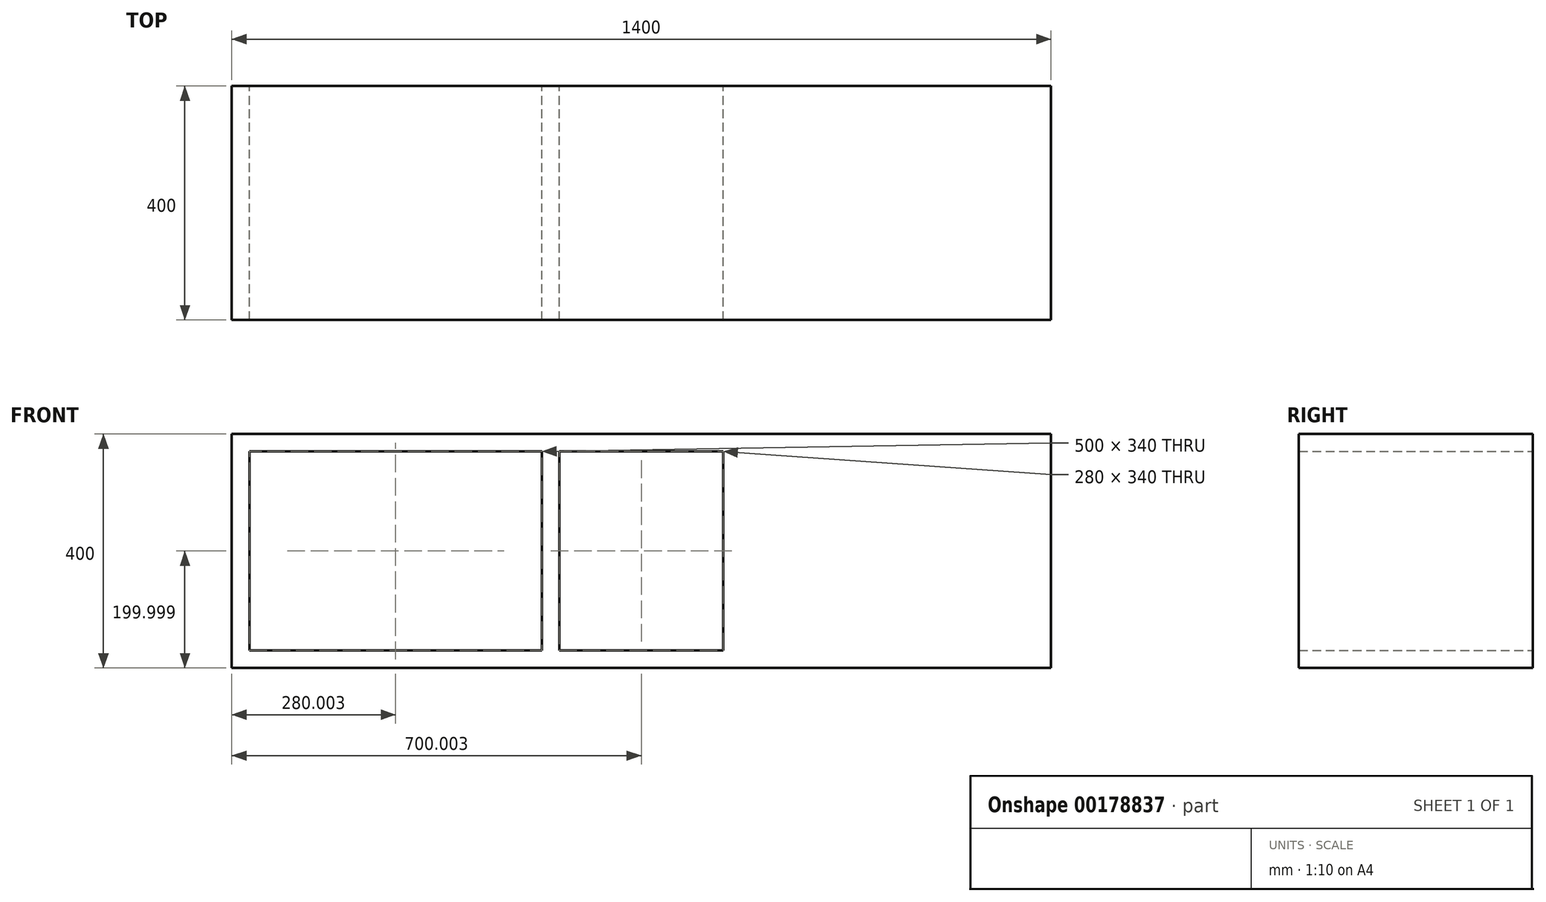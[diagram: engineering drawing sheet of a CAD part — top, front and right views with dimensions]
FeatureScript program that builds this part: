
annotation { "Feature Type Name" : "Feature", "Feature Type Description" : "" }
export const myFeature = defineFeature(function(context is Context, id is Id, definition is map)
    precondition{}
    {
        {
            var Q0;
            Q0=qCreatedBy(makeId("Front.planeOp"),FACE);
            var sketch = newSketch(context, id + "F0", { "sketchPlane" : qUnion([Q0])});
            skLineSegment(sketch, "E0.bottom", {"start": v(-701.84, 183.72) * mm, "end": v(698.16, 183.72) * mm});
            skLineSegment(sketch, "E0.top", {"start": v(-701.84, -216.28) * mm, "end": v(698.16, -216.28) * mm});
            skLineSegment(sketch, "E0.left", {"start": v(-701.84, 183.72) * mm, "end": v(-701.84, -216.28) * mm});
            skLineSegment(sketch, "E0.right", {"start": v(698.16, 183.72) * mm, "end": v(698.16, -216.28) * mm});
            skLineSegment(sketch, "E1.bottom", {"start": v(-701.84, -216.28) * mm, "end": v(-551.84, -216.28) * mm});
            skLineSegment(sketch, "E1.top", {"start": v(-701.84, -246.28) * mm, "end": v(-551.84, -246.28) * mm});
            skLineSegment(sketch, "E1.left", {"start": v(-701.84, -216.28) * mm, "end": v(-701.84, -246.28) * mm});
            skLineSegment(sketch, "E1.right", {"start": v(-551.84, -216.28) * mm, "end": v(-551.84, -246.28) * mm});
            skLineSegment(sketch, "E2.bottom", {"start": v(698.16, -216.28) * mm, "end": v(548.16, -216.28) * mm});
            skLineSegment(sketch, "E2.top", {"start": v(698.16, -246.28) * mm, "end": v(548.16, -246.28) * mm});
            skLineSegment(sketch, "E2.left", {"start": v(698.16, -216.28) * mm, "end": v(698.16, -246.28) * mm});
            skLineSegment(sketch, "E2.right", {"start": v(548.16, -216.28) * mm, "end": v(548.16, -246.28) * mm});
            skLineSegment(sketch, "E3.bottom", {"start": v(668.16, 153.72) * mm, "end": v(168.16, 153.72) * mm});
            skLineSegment(sketch, "E3.top", {"start": v(668.16, -186.28) * mm, "end": v(168.16, -186.28) * mm});
            skLineSegment(sketch, "E3.left", {"start": v(668.16, 153.72) * mm, "end": v(668.16, -186.28) * mm});
            skLineSegment(sketch, "E3.right", {"start": v(168.16, 153.72) * mm, "end": v(168.16, -186.28) * mm});
            skLineSegment(sketch, "E4.bottom", {"start": v(138.16, 153.72) * mm, "end": v(-141.84, 153.72) * mm});
            skLineSegment(sketch, "E4.top", {"start": v(138.16, -186.28) * mm, "end": v(-141.84, -186.28) * mm});
            skLineSegment(sketch, "E4.left", {"start": v(138.16, 153.72) * mm, "end": v(138.16, -186.28) * mm});
            skLineSegment(sketch, "E4.right", {"start": v(-141.84, 153.72) * mm, "end": v(-141.84, -186.28) * mm});
            skLineSegment(sketch, "E5.bottom", {"start": v(-671.84, 153.72) * mm, "end": v(-171.84, 153.72) * mm});
            skLineSegment(sketch, "E5.top", {"start": v(-671.84, -186.28) * mm, "end": v(-171.84, -186.28) * mm});
            skLineSegment(sketch, "E5.left", {"start": v(-671.84, 153.72) * mm, "end": v(-671.84, -186.28) * mm});
            skLineSegment(sketch, "E5.right", {"start": v(-171.84, 153.72) * mm, "end": v(-171.84, -186.28) * mm});
            skLineSegment(sketch, "E6.right", {"start": v(698.16, 153.72) * mm, "end": v(698.16, -186.28) * mm});
            skLineSegment(sketch, "E7.left", {"start": v(-701.84, 143.84) * mm, "end": v(-701.84, 143.72) * mm});
            skLineSegment(sketch, "E7.right", {"start": v(-671.84, 153.84) * mm, "end": v(-671.84, 153.72) * mm});
            skSolve(sketch);
        }
        {
            var Q0;
            {var subQ4=sQuery(id+"F0.wireOp",EDGE,"E0.bottom");Q0=makeQuery(id+"F0.imprint","IMPRINT",FACE,{"disambiguationData":[TD([[makeQuery(id+"F0.imprint","IMPRINT",EDGE,{"derivedFrom":subQ4}),-1.0]])]});}
            var Q1;
            Q1=makeQuery(id+"F0.imprint","IMPRINT",FACE,{"disambiguationData":[TD([[makeQuery(id+"F0.imprint","IMPRINT",EDGE,{"derivedFrom":sQuery(id+"F0.wireOp",EDGE,"E2.bottom")}),1.0]])]});
            var Q2;
            Q2=makeQuery(id+"F0.imprint","IMPRINT",FACE,{"disambiguationData":[TD([[makeQuery(id+"F0.imprint","IMPRINT",EDGE,{"derivedFrom":sQuery(id+"F0.wireOp",EDGE,"E3.bottom")}),1.0]])]});
            var Q3;
            Q3=makeQuery(id+"F0.imprint","IMPRINT",FACE,{"disambiguationData":[TD([[makeQuery(id+"F0.imprint","IMPRINT",EDGE,{"derivedFrom":sQuery(id+"F0.wireOp",EDGE,"E1.bottom")}),-1.0]])]});
            extrude(context, id + "F1", {"entities" : qUnion([Q0, Q1, Q2, Q3]), "depth" : 400 * mm});
        }
    });
